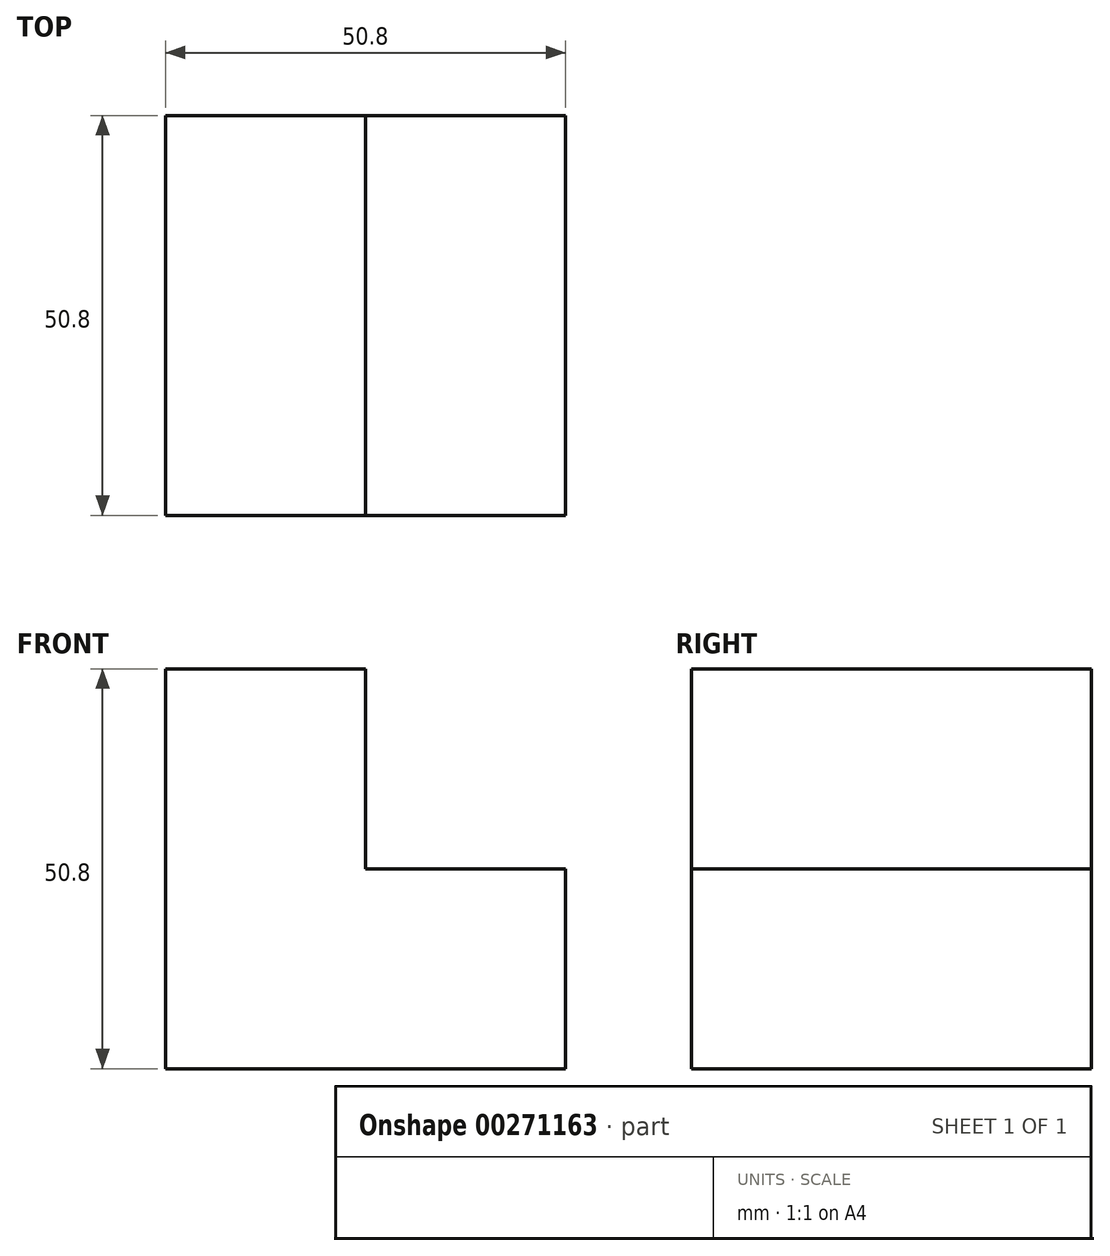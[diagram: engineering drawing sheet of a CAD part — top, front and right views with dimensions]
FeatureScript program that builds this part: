
annotation { "Feature Type Name" : "Feature", "Feature Type Description" : "" }
export const myFeature = defineFeature(function(context is Context, id is Id, definition is map)
    precondition{}
    {
        {
            var Q0;
            Q0=qCreatedBy(makeId("Front.planeOp"),FACE);
            var sketch = newSketch(context, id + "F0", { "sketchPlane" : qUnion([Q0])});
            skLineSegment(sketch, "E0", {"start": v(0, 0) * mm, "end": v(-50.8, 0) * mm});
            skLineSegment(sketch, "E1", {"start": v(-50.8, 0) * mm, "end": v(-50.8, 50.8) * mm});
            skLineSegment(sketch, "E2", {"start": v(-50.8, 50.8) * mm, "end": v(-25.4, 50.8) * mm});
            skLineSegment(sketch, "E3", {"start": v(0, 0) * mm, "end": v(0, 25.4) * mm});
            skLineSegment(sketch, "E4", {"start": v(0, 25.4) * mm, "end": v(-25.4, 25.4) * mm});
            skLineSegment(sketch, "E5", {"start": v(-25.4, 25.4) * mm, "end": v(-25.4, 50.8) * mm});
            skSolve(sketch);
        }
        {
            var Q0;
            Q0 = qSketchRegion(id + "F0", true);
            extrude(context, id + "F1", {"entities" : qUnion([Q0]), "depth" : 50.8 * mm});
        }
    });
